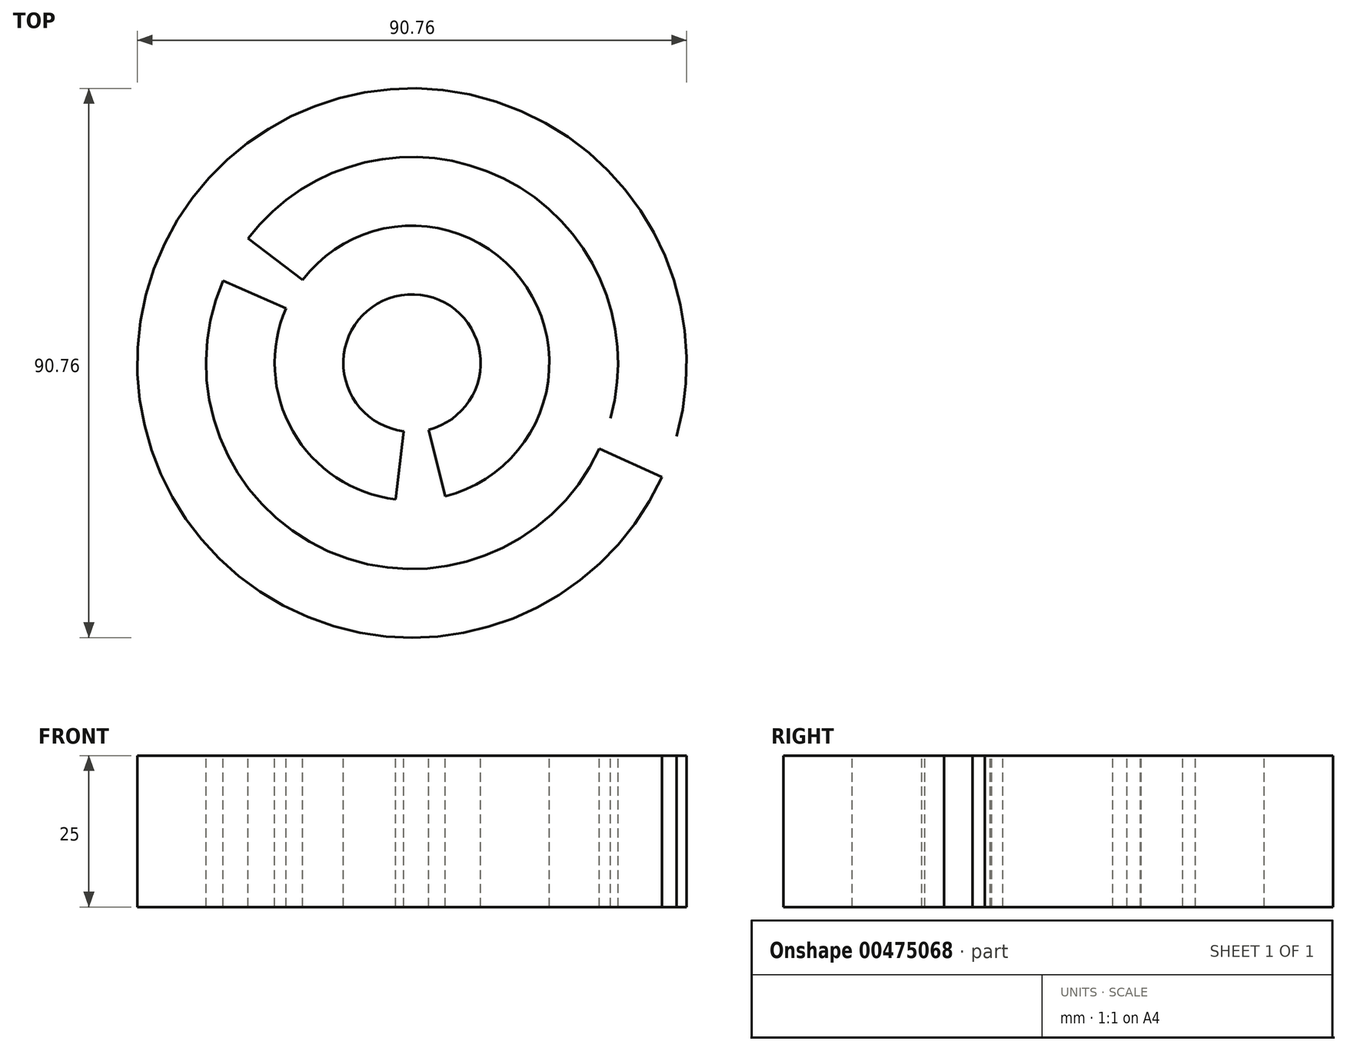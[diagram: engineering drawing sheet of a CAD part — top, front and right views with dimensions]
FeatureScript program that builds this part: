
annotation { "Feature Type Name" : "Feature", "Feature Type Description" : "" }
export const myFeature = defineFeature(function(context is Context, id is Id, definition is map)
    precondition{}
    {
        {
            var Q0;
            Q0=qCreatedBy(makeId("Top.planeOp"),FACE);
            var sketch = newSketch(context, id + "F0", { "sketchPlane" : qUnion([Q0])});
            skArc(sketch, "E0", {"start": v(43.72, -12.15) * mm, "mid": v(-42.63, 15.54) * mm, "end": v(41.28, -18.84) * mm});
            skArc(sketch, "E1", {"start": v(32.8, -9.1) * mm, "mid": v(15.12, 30.49) * mm, "end": v(-27.1, 20.6) * mm});
            skArc(sketch, "E2", {"start": v(-20.8, 9.05) * mm, "mid": v(-19.7, -11.27) * mm, "end": v(-2.73, -22.52) * mm});
            skArc(sketch, "E3", {"start": v(2.75, -11) * mm, "mid": v(-0.7, 11.32) * mm, "end": v(-1.37, -11.26) * mm});
            skLineSegment(sketch, "E4", {"start": v(-20.8, 9.05) * mm, "end": v(-31.21, 13.57) * mm});
            skLineSegment(sketch, "E5", {"start": v(-1.37, -11.26) * mm, "end": v(-2.73, -22.52) * mm});
            skLineSegment(sketch, "E6.trimOffspring", {"start": v(30.96, -14.13) * mm, "end": v(41.28, -18.84) * mm});
            skLineSegment(sketch, "E7", {"start": v(-27.1, 20.6) * mm, "end": v(-18.06, 13.73) * mm});
            skArc(sketch, "E8.trimOffspring", {"start": v(-31.21, 13.57) * mm, "mid": v(-13.85, -31.09) * mm, "end": v(30.96, -14.13) * mm});
            skLineSegment(sketch, "E9", {"start": v(2.75, -11) * mm, "end": v(5.5, -22.01) * mm});
            skArc(sketch, "E10.trimOffspring", {"start": v(5.5, -22.01) * mm, "mid": v(18.94, 12.49) * mm, "end": v(-18.06, 13.73) * mm});
            skCircle(sketch, "E11", {"center": v(32.8, -9.1) * mm, "radius": 2.54 * mm});
            skCircle(sketch, "E12", {"center": v(43.72, -12.15) * mm, "radius": 2.29 * mm});
            skSolve(sketch);
        }
        {
            var Q0;
            Q0=makeQuery(id+"F0.imprint","IMPRINT",FACE,{"disambiguationData":[TD([[makeQuery(id+"F0.imprint","IMPRINT",EDGE,{"derivedFrom":sQuery(id+"F0.wireOp",EDGE,"E11")}),1.0]])]});
            var Q1;
            Q1=makeQuery(id+"F0.imprint","IMPRINT",FACE,{"disambiguationData":[TD([[makeQuery(id+"F0.imprint","IMPRINT",EDGE,{"derivedFrom":sQuery(id+"F0.wireOp",EDGE,"E12")}),1.0]])]});
            var Q2;
            Q2=sQuery(id+"F0.wireOp",EDGE,"E0");
            var Q3;
            Q3=sQuery(id+"F0.wireOp",EDGE,"E1");
            var Q4;
            Q4=sQuery(id+"F0.wireOp",EDGE,"E2");
            var Q5;
            Q5=sQuery(id+"F0.wireOp",EDGE,"E3");
            var Q6;
            Q6=sQuery(id+"F0.wireOp",EDGE,"E4");
            var Q7;
            Q7=sQuery(id+"F0.wireOp",EDGE,"E5");
            var Q8;
            Q8=sQuery(id+"F0.wireOp",EDGE,"E6.trimOffspring");
            var Q9;
            Q9=sQuery(id+"F0.wireOp",EDGE,"E7");
            var Q10;
            Q10=sQuery(id+"F0.wireOp",EDGE,"E8.trimOffspring");
            var Q11;
            Q11=sQuery(id+"F0.wireOp",EDGE,"E9");
            var Q12;
            Q12=sQuery(id+"F0.wireOp",EDGE,"E10.trimOffspring");
            extrude(context, id + "F1", {"entities" : qUnion([Q0, Q1]), "bodyType" : ToolBodyType.SURFACE, "surfaceEntities" : qUnion([Q2, Q3, Q4, Q5, Q6, Q7, Q8, Q9, Q10, Q11, Q12]), "depth" : 25 * mm});
        }
    });
